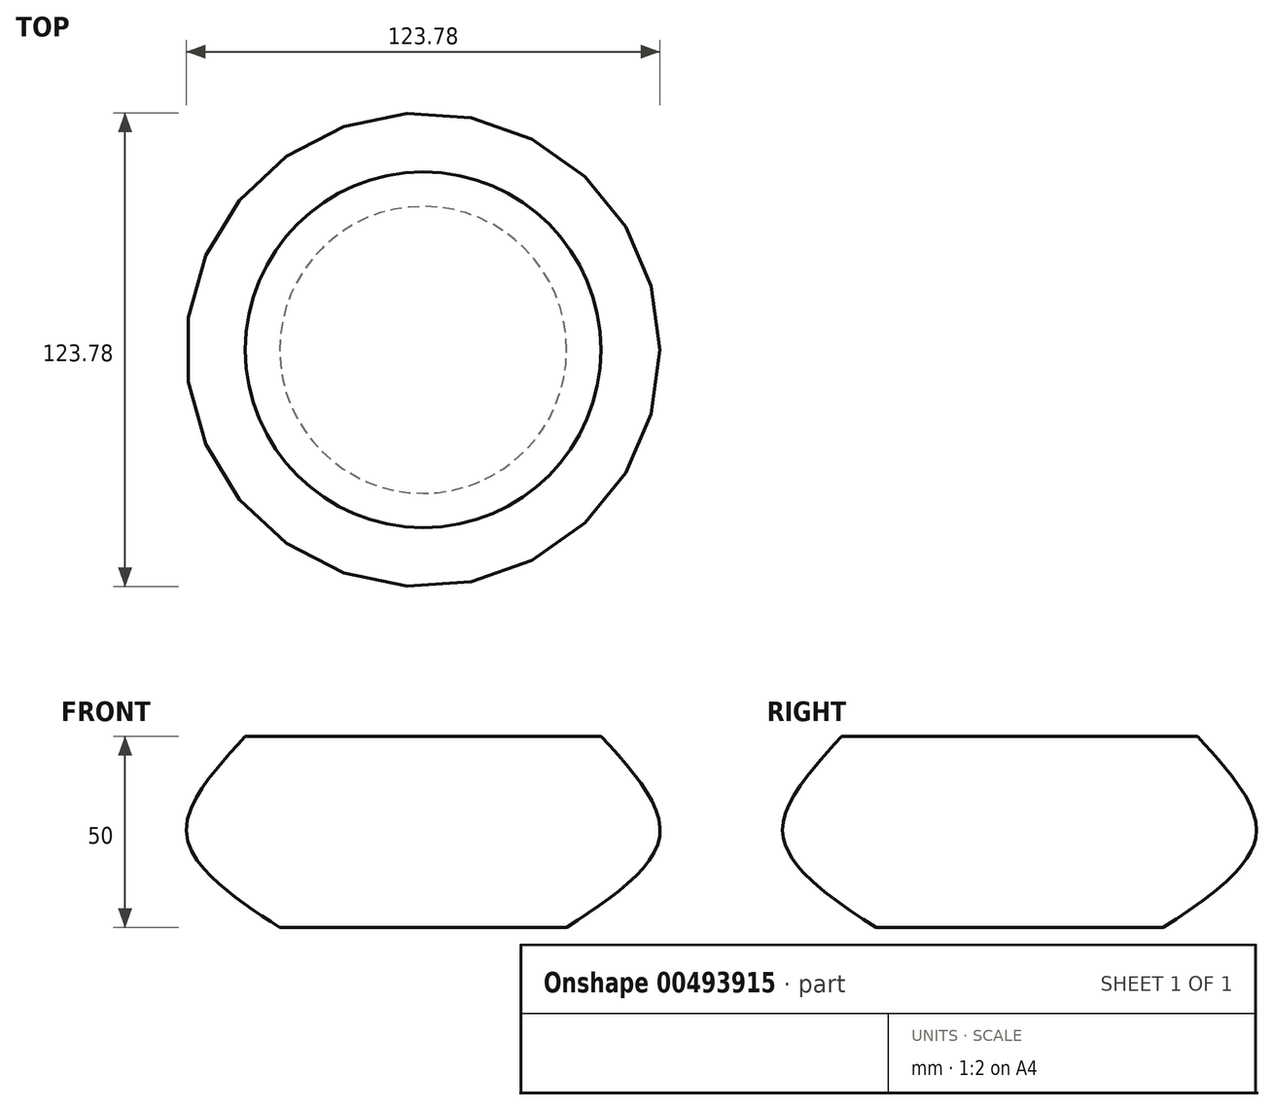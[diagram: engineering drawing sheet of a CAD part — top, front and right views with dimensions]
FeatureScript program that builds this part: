
annotation { "Feature Type Name" : "Feature", "Feature Type Description" : "" }
export const myFeature = defineFeature(function(context is Context, id is Id, definition is map)
    precondition{}
    {
        {
            var Q0;
            Q0=qCreatedBy(makeId("Top.planeOp"),FACE);
            cPlane(context, id + "F0", {"entities" : qUnion([Q0]), "cplaneType" : CPlaneType.OFFSET, "offset" : 25 * mm, "width" : 150 * mm, "height" : 150 * mm});
        }
        {
            var Q0;
            Q0=qCreatedBy(id+"F0.planeOp",FACE);
            cPlane(context, id + "F1", {"entities" : qUnion([Q0]), "cplaneType" : CPlaneType.OFFSET, "offset" : 25 * mm, "width" : 150 * mm, "height" : 150 * mm});
        }
        {
            var Q0;
            Q0=qCreatedBy(makeId("Top.planeOp"),FACE);
            var sketch = newSketch(context, id + "F2", { "sketchPlane" : qUnion([Q0])});
            skCircle(sketch, "E0", {"center": v(0, 0) * mm, "radius": 37.46 * mm});
            skSolve(sketch);
        }
        {
            var Q0;
            Q0=qCreatedBy(id+"F0.planeOp",FACE);
            var sketch = newSketch(context, id + "F3", { "sketchPlane" : qUnion([Q0])});
            skCircle(sketch, "E1", {"center": v(0, 0) * mm, "radius": 61.88 * mm});
            skSolve(sketch);
        }
        {
            var Q0;
            Q0=qCreatedBy(id+"F1.planeOp",FACE);
            var sketch = newSketch(context, id + "F4", { "sketchPlane" : qUnion([Q0])});
            skCircle(sketch, "E2", {"center": v(0, 0) * mm, "radius": 46.45 * mm});
            skSolve(sketch);
        }
        {
            var Q0;
            Q0=makeQuery(id+"F4.imprint","IMPRINT",FACE,{"disambiguationData":[TD([[makeQuery(id+"F4.imprint","IMPRINT",EDGE,{"derivedFrom":sQuery(id+"F4.wireOp",EDGE,"E2")}),1.0]])]});
            var Q1;
            Q1=makeQuery(id+"F3.imprint","IMPRINT",FACE,{"disambiguationData":[TD([[makeQuery(id+"F3.imprint","IMPRINT",EDGE,{"derivedFrom":sQuery(id+"F3.wireOp",EDGE,"E1")}),1.0]])]});
            var Q2;
            Q2=makeQuery(id+"F2.imprint","IMPRINT",FACE,{"disambiguationData":[TD([[makeQuery(id+"F2.imprint","IMPRINT",EDGE,{"derivedFrom":sQuery(id+"F2.wireOp",EDGE,"E0")}),1.0]])]});
            loft(context, id + "F5", {"sheetProfilesArray" : [{ "sheetProfileEntities" : qUnion([Q0]) }, { "sheetProfileEntities" : qUnion([Q1]) }, { "sheetProfileEntities" : qUnion([Q2]) }]});
        }
    });
